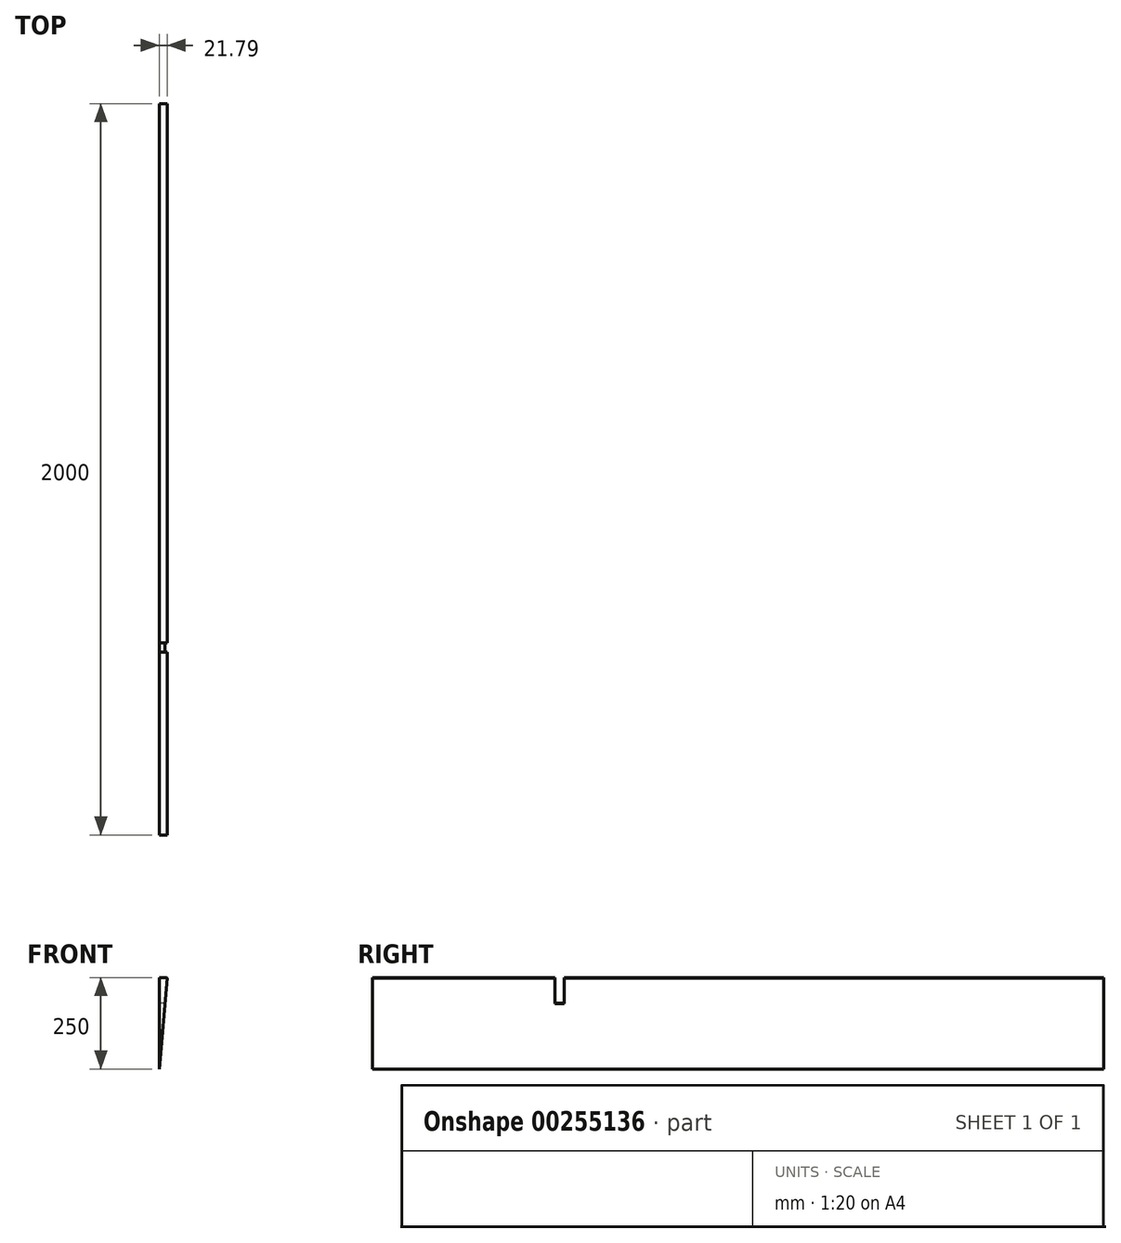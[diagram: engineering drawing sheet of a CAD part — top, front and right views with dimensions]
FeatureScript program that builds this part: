
annotation { "Feature Type Name" : "Feature", "Feature Type Description" : "" }
export const myFeature = defineFeature(function(context is Context, id is Id, definition is map)
    precondition{}
    {
        {
            var Q0;
            Q0=qCreatedBy(makeId("Front.planeOp"),FACE);
            var sketch = newSketch(context, id + "F0", { "sketchPlane" : qUnion([Q0])});
            skCircle(sketch, "E0", {"center": v(0, 0) * mm, "radius": 250 * mm});
            skSolve(sketch);
        }
        {
            var Q0;
            Q0=makeQuery(id+"F0.imprint","IMPRINT",FACE,{"disambiguationData":[TD([[makeQuery(id+"F0.imprint","IMPRINT",EDGE,{"derivedFrom":sQuery(id+"F0.wireOp",EDGE,"E0")}),1.0]])]});
            extrude(context, id + "F1", {"entities" : qUnion([Q0]), "depth" : 2000 * mm});
        }
        {
            var Q0;
            Q0=makeQuery(id+"F1.opExtrude","CAP_FACE",FACE,{"disambiguationData":[OSD([sQuery(id+"F0.wireOp",EDGE,"E0")])],"isStart":false});
            cPlane(context, id + "F2", {"entities" : qUnion([Q0]), "cplaneType" : CPlaneType.OFFSET, "offset" : 500 * mm, "oppositeDirection" : true, "width" : 150 * mm, "height" : 150 * mm});
        }
        {
            var Q0;
            Q0=qCreatedBy(id+"F2.planeOp",FACE);
            var sketch = newSketch(context, id + "F3", { "sketchPlane" : qUnion([Q0])});
            skEllipse(sketch, "E1", {"center": v(0, 0) * mm, "majorRadius": 130 * mm, "minorRadius": 180 * mm, "majorAxis": v(1, 0)});
            skLineSegment(sketch, "E2.bottom", {"start": v(-366.34, 256.7) * mm, "end": v(520.5, 256.7) * mm});
            skLineSegment(sketch, "E2.top", {"start": v(-366.34, -267.16) * mm, "end": v(520.5, -267.16) * mm});
            skLineSegment(sketch, "E2.left", {"start": v(-366.34, 256.7) * mm, "end": v(-366.34, -267.16) * mm});
            skLineSegment(sketch, "E2.right", {"start": v(520.5, 256.7) * mm, "end": v(520.5, -267.16) * mm});
            skSolve(sketch);
        }
        {
            var Q0;
            Q0=makeQuery(id+"F3.imprint","IMPRINT",FACE,{"disambiguationData":[TD([[makeQuery(id+"F3.imprint","IMPRINT",EDGE,{"derivedFrom":sQuery(id+"F3.wireOp",EDGE,"E1")}),-1.0]])]});
            extrude(context, id + "F4", {"entities" : qUnion([Q0]), "operationType" : NewBodyOperationType.REMOVE, "oppositeDirection" : true, "depth" : 25 * mm});
        }
        {
            var Q0;
            Q0=makeQuery(id+"F1.opExtrude","CAP_FACE",FACE,{"disambiguationData":[OSD([sQuery(id+"F0.wireOp",EDGE,"E0")])],"isStart":false});
            var sketch = newSketch(context, id + "F5", { "sketchPlane" : qUnion([Q0])});
            skLineSegment(sketch, "E3", {"start": v(0, 0) * mm, "end": v(0, 250) * mm});
            skLineSegment(sketch, "E4", {"start": v(0, 0) * mm, "end": v(21.79, 249.05) * mm});
            skSolve(sketch);
        }
        {
            var Q0;
            {var subQ0=sQuery(id+"F5.wireOp",EDGE,"E3");Q0=makeQuery(id+"F5.imprint","IMPRINT",FACE,{"disambiguationData":[TD([[makeQuery(id+"F5.imprint","IMPRINT",EDGE,{"derivedFrom":subQ0}),-1.0]])]});}
            extrude(context, id + "F6", {"entities" : qUnion([Q0]), "operationType" : NewBodyOperationType.INTERSECT, "oppositeDirection" : true, "depth" : 2000 * mm});
        }
    });
